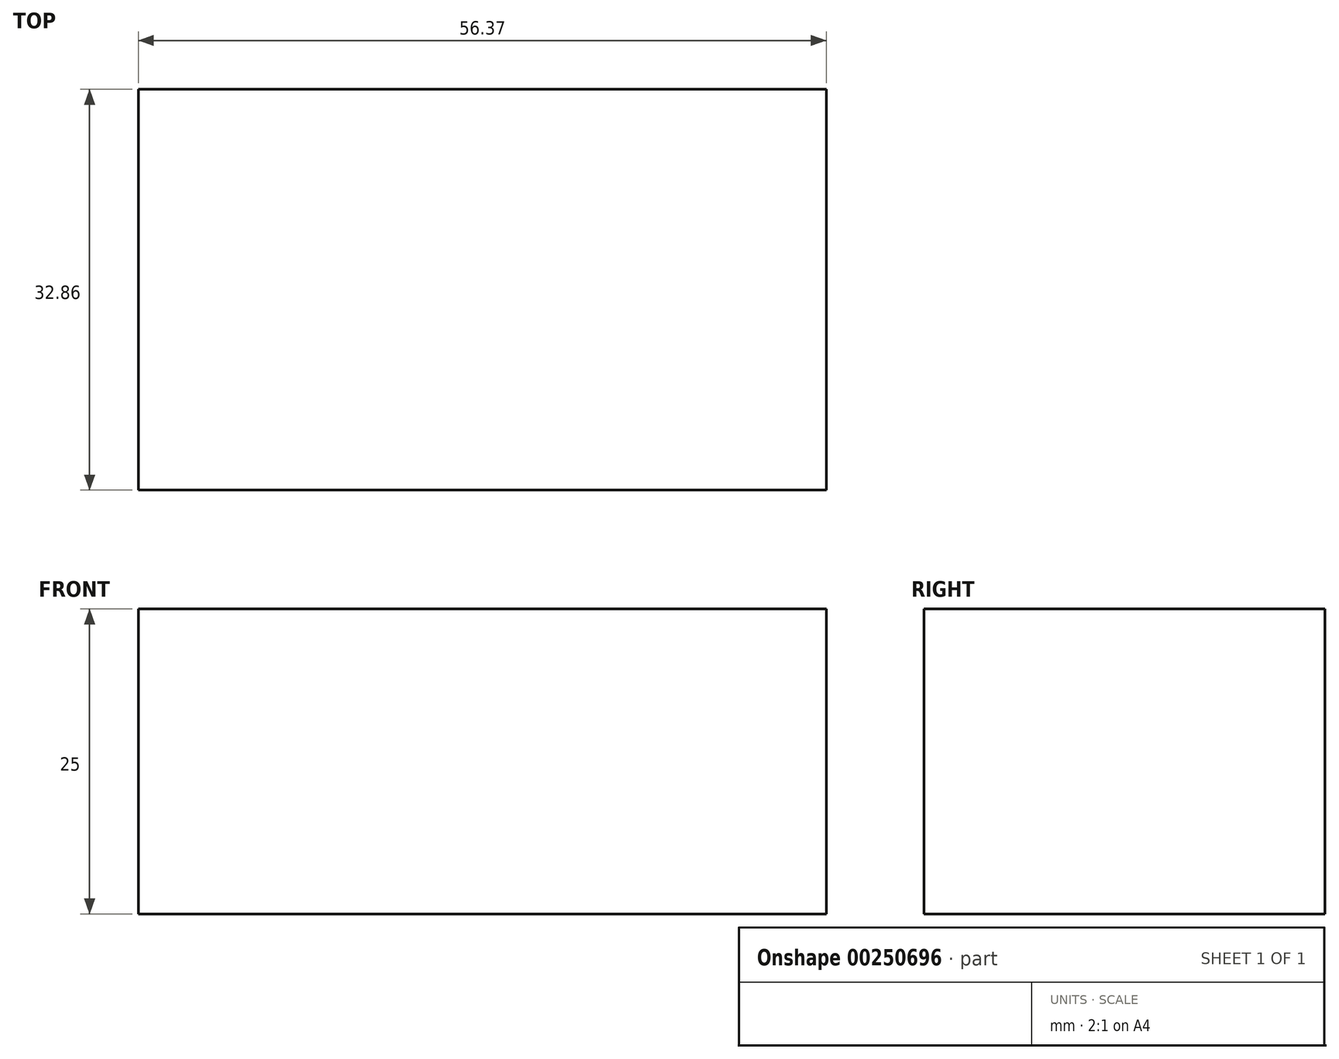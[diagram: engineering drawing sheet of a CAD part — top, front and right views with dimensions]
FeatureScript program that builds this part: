
annotation { "Feature Type Name" : "Feature", "Feature Type Description" : "" }
export const myFeature = defineFeature(function(context is Context, id is Id, definition is map)
    precondition{}
    {
        {
            var Q0;
            Q0=qCreatedBy(makeId("Top.planeOp"),FACE);
            var sketch = newSketch(context, id + "F0", { "sketchPlane" : qUnion([Q0])});
            skLineSegment(sketch, "E0.bottom", {"start": v(-66.57, 43.62) * mm, "end": v(-10.2, 43.62) * mm});
            skLineSegment(sketch, "E0.top", {"start": v(-66.57, 10.76) * mm, "end": v(-10.2, 10.76) * mm});
            skLineSegment(sketch, "E0.left", {"start": v(-66.57, 43.62) * mm, "end": v(-66.57, 10.76) * mm});
            skLineSegment(sketch, "E0.right", {"start": v(-10.2, 43.62) * mm, "end": v(-10.2, 10.76) * mm});
            skSolve(sketch);
        }
        {
            var Q0;
            Q0=sQuery(id+"F0.wireOp",EDGE,"E0.left");
            var Q1;
            Q1=sQuery(id+"F0.wireOp",EDGE,"E0.top");
            var Q2;
            Q2=sQuery(id+"F0.wireOp",EDGE,"E0.right");
            var Q3;
            Q3=sQuery(id+"F0.wireOp",EDGE,"E0.bottom");
            extrude(context, id + "F1", {"bodyType" : ToolBodyType.SURFACE, "surfaceEntities" : qUnion([Q0, Q1, Q2, Q3]), "depth" : 25 * mm});
        }
    });
